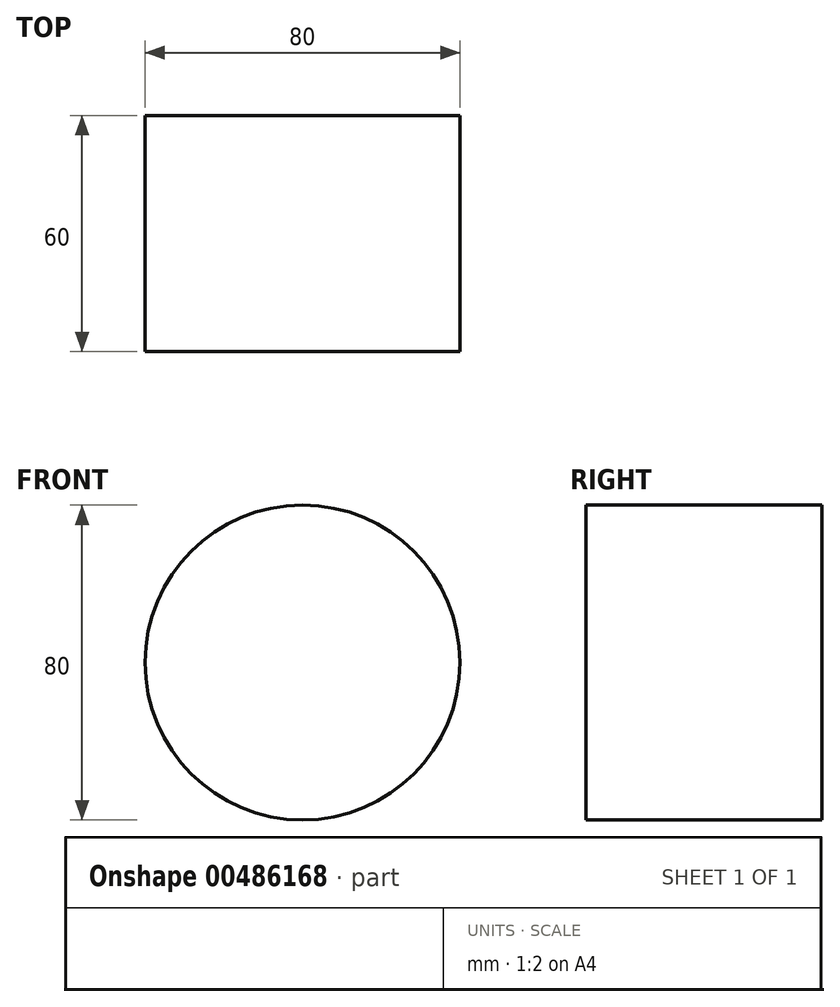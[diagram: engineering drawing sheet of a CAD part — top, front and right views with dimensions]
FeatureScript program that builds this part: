
annotation { "Feature Type Name" : "Feature", "Feature Type Description" : "" }
export const myFeature = defineFeature(function(context is Context, id is Id, definition is map)
    precondition{}
    {
        {
            var Q0;
            Q0=qCreatedBy(makeId("Front.planeOp"),FACE);
            var sketch = newSketch(context, id + "F0", { "sketchPlane" : qUnion([Q0])});
            skCircle(sketch, "E0", {"center": v(0, 0) * mm, "radius": 40 * mm});
            skSolve(sketch);
        }
        {
            var Q0;
            Q0 = qSketchRegion(id + "F0", true);
            extrude(context, id + "F1", {"entities" : qUnion([Q0]), "depth" : 60 * mm});
        }
    });
